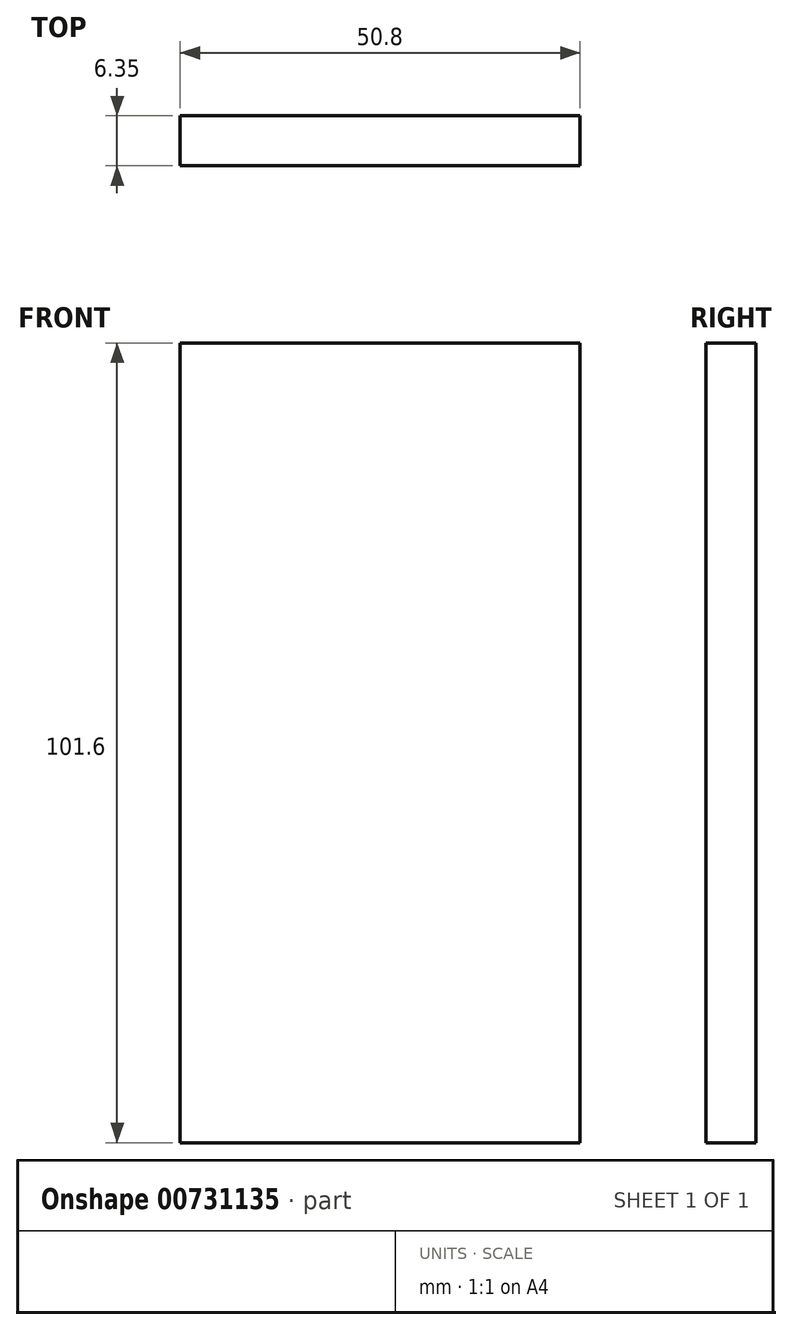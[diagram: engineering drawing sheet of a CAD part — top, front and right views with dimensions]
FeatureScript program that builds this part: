
annotation { "Feature Type Name" : "Feature", "Feature Type Description" : "" }
export const myFeature = defineFeature(function(context is Context, id is Id, definition is map)
    precondition{}
    {
        {
            var Q0;
            Q0=qCreatedBy(makeId("Front.planeOp"),FACE);
            var sketch = newSketch(context, id + "F0", { "sketchPlane" : qUnion([Q0])});
            skLineSegment(sketch, "E0.bottom", {"start": v(-35.28, 50.43) * mm, "end": v(15.52, 50.43) * mm});
            skLineSegment(sketch, "E0.top", {"start": v(-35.28, -51.17) * mm, "end": v(15.52, -51.17) * mm});
            skLineSegment(sketch, "E0.left", {"start": v(-35.28, 50.43) * mm, "end": v(-35.28, -51.17) * mm});
            skLineSegment(sketch, "E0.right", {"start": v(15.52, 50.43) * mm, "end": v(15.52, -51.17) * mm});
            skSolve(sketch);
        }
        {
            var Q0;
            Q0 = qSketchRegion(id + "F0", true);
            extrude(context, id + "F1", {"entities" : qUnion([Q0]), "depth" : 6.35 * mm, "offsetDistance" : 25.4 * mm});
        }
    });
